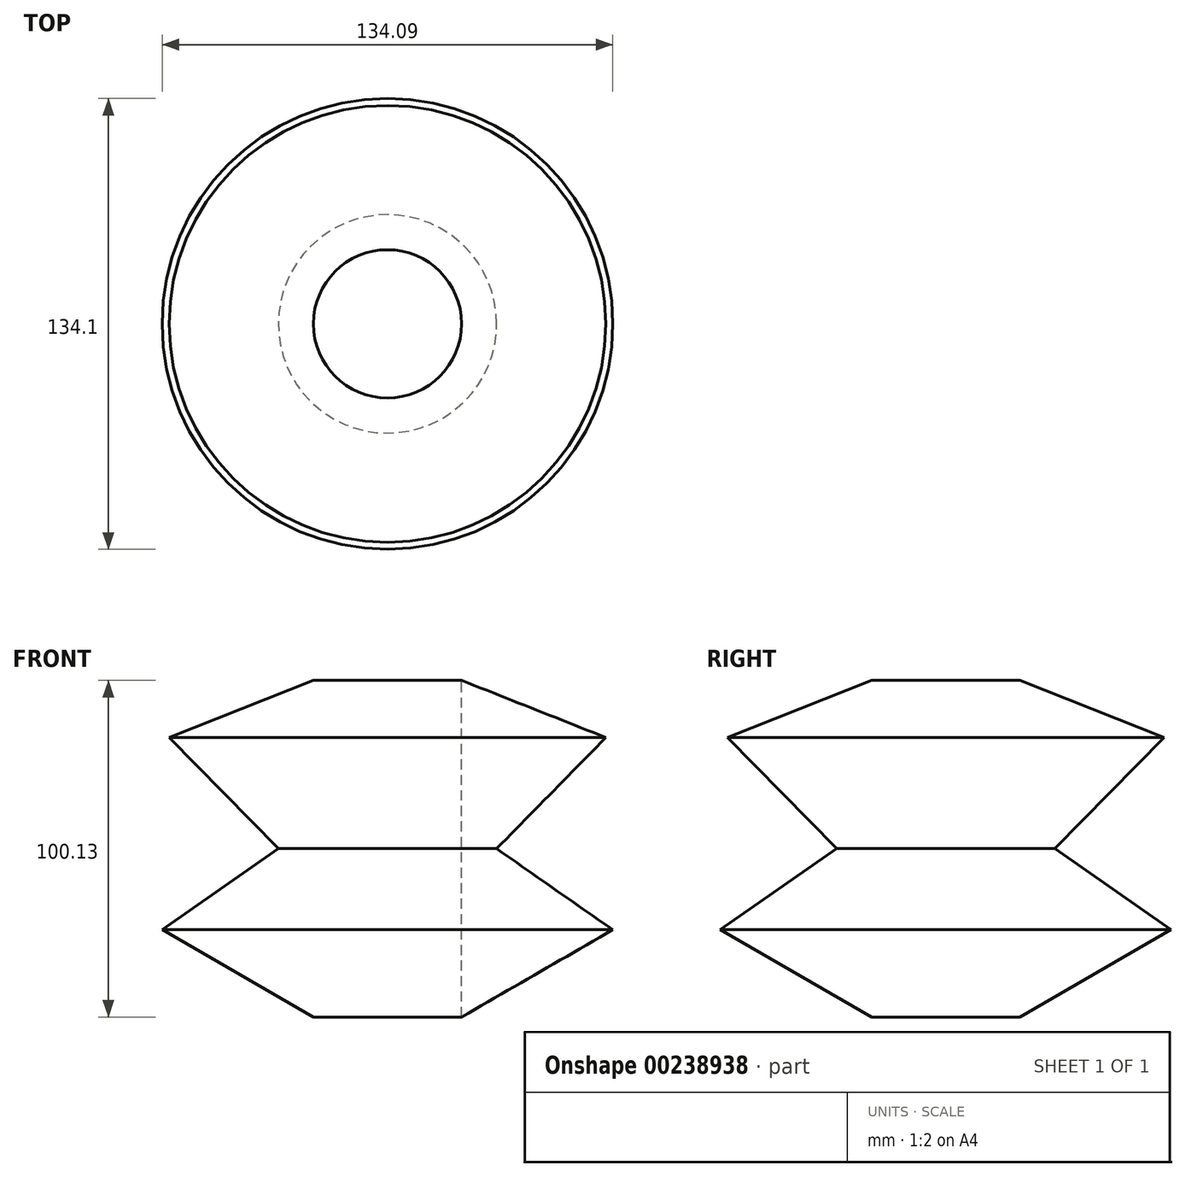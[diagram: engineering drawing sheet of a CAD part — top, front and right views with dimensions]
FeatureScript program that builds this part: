
annotation { "Feature Type Name" : "Feature", "Feature Type Description" : "" }
export const myFeature = defineFeature(function(context is Context, id is Id, definition is map)
    precondition{}
    {
        {
            var Q0;
            Q0=qCreatedBy(makeId("Front.planeOp"),FACE);
            var sketch = newSketch(context, id + "F0", { "sketchPlane" : qUnion([Q0])});
            skLineSegment(sketch, "E0", {"start": v(-24.29, 42.17) * mm, "end": v(-24.29, -57.96) * mm});
            skLineSegment(sketch, "E1", {"start": v(-24.29, 42.17) * mm, "end": v(18.62, 25.18) * mm});
            skLineSegment(sketch, "E2", {"start": v(18.62, 25.18) * mm, "end": v(-13.86, -7.9) * mm});
            skLineSegment(sketch, "E3", {"start": v(-13.86, -7.9) * mm, "end": v(20.71, -32.03) * mm});
            skLineSegment(sketch, "E4", {"start": v(20.71, -32.03) * mm, "end": v(-24.29, -57.96) * mm});
            skLineSegment(sketch, "E5", {"start": v(-46.34, 42.17) * mm, "end": v(-46.34, -57.96) * mm});
            skSolve(sketch);
        }
        {
            var Q0;
            Q0=makeQuery(id+"F0.imprint","IMPRINT",FACE,{"disambiguationData":[TD([[makeQuery(id+"F0.imprint","IMPRINT",EDGE,{"derivedFrom":sQuery(id+"F0.wireOp",EDGE,"E0")}),1.0]])]});
            var Q1;
            Q1=sQuery(id+"F0.wireOp",EDGE,"E5");
            revolve(context, id + "F1", {"entities" : qUnion([Q0]), "axis" : qUnion([Q1]), "revolveType" : RevolveType.FULL});
        }
    });
